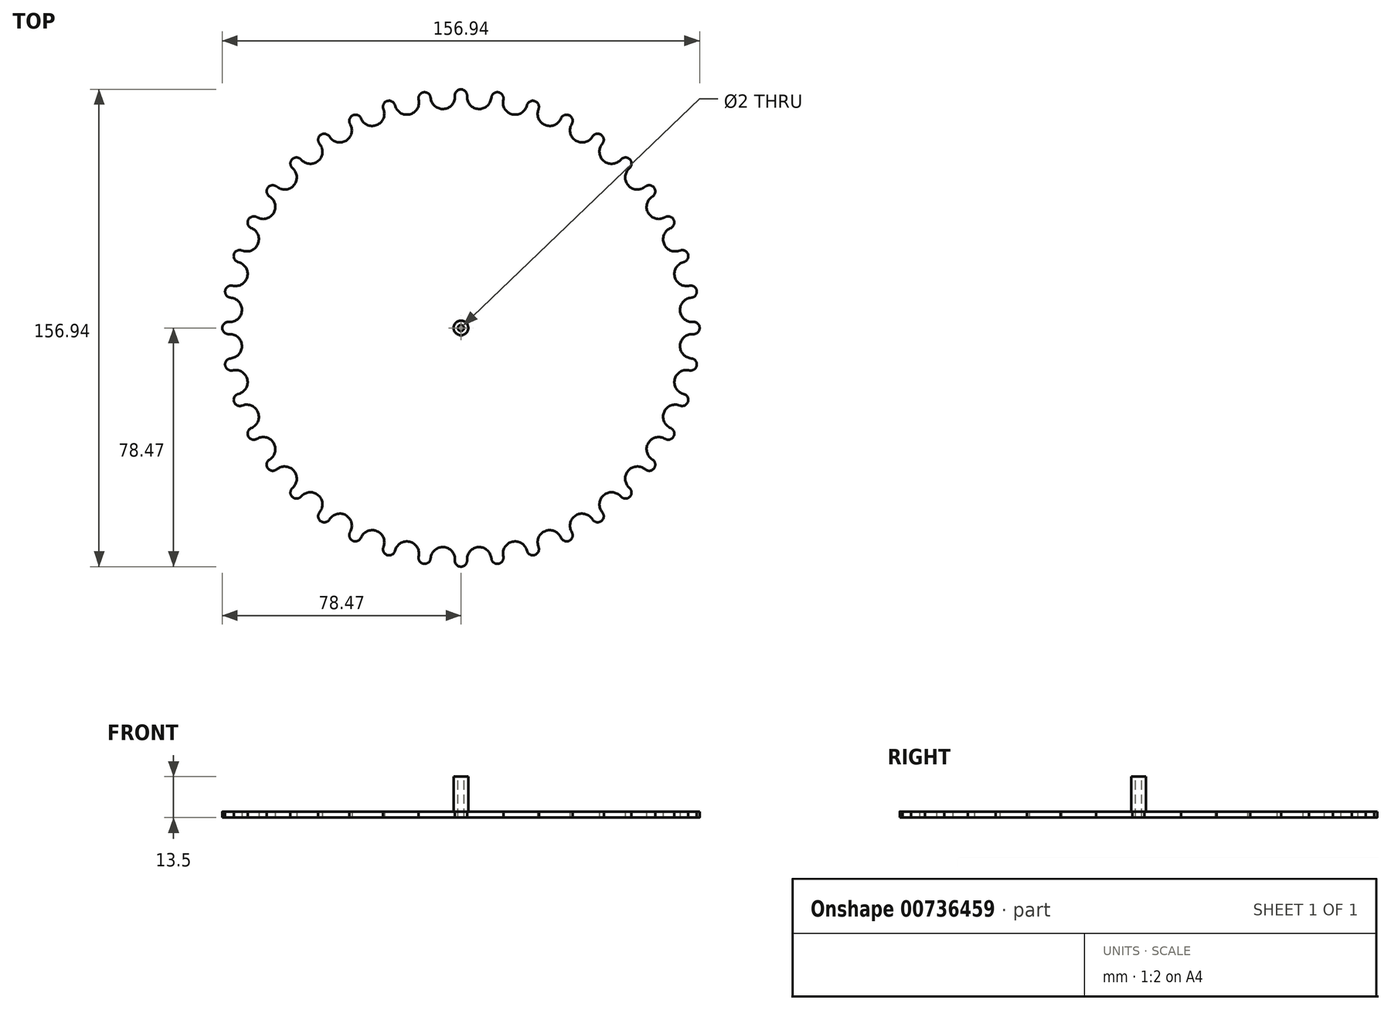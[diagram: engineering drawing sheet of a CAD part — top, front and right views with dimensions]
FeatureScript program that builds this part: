
annotation { "Feature Type Name" : "Feature", "Feature Type Description" : "" }
export const myFeature = defineFeature(function(context is Context, id is Id, definition is map)
    precondition{}
    {
        {
            var Q0;
            Q0=qCreatedBy(makeId("Top.planeOp"),FACE);
            var sketch = newSketch(context, id + "F0", { "sketchPlane" : qUnion([Q0])});
            skArc(sketch, "E0", {"start": v(2, 76.47) * mm, "mid": v(0, 78.47) * mm, "end": v(-2, 76.47) * mm});
            skLineSegment(sketch, "E1", {"start": v(2, 76.47) * mm, "end": v(2, 76) * mm});
            skLineSegment(sketch, "E2", {"start": v(-2, 76.47) * mm, "end": v(-2, 76) * mm});
            skLineSegment(sketch, "E3", {"start": v(-5.98, 76) * mm, "end": v(-5.67, 72.03) * mm, "construction": true});
            skArc(sketch, "E4", {"start": v(-5.67, 72.03) * mm, "mid": v(-3.06, 73.3) * mm, "end": v(-2, 76) * mm});
            skLineSegment(sketch, "E5", {"start": v(-5.67, 72.03) * mm, "end": v(-4.67, 72.11) * mm, "construction": true});
            skLineSegment(sketch, "E6", {"start": v(0, 0) * mm, "end": v(-5.67, 72.03) * mm});
            skCircle(sketch, "E7.cCircle", {"center": v(0, 0) * mm, "radius": 76.47 * mm, "construction": true});
            skLineSegment(sketch, "E7.0", {"start": v(0, 76.47) * mm, "end": v(11.96, 75.53) * mm, "construction": true});
            skLineSegment(sketch, "E7.1", {"start": v(11.96, 75.53) * mm, "end": v(23.63, 72.73) * mm, "construction": true});
            skLineSegment(sketch, "E7.2", {"start": v(23.63, 72.73) * mm, "end": v(34.72, 68.14) * mm, "construction": true});
            skLineSegment(sketch, "E7.3", {"start": v(34.72, 68.14) * mm, "end": v(44.95, 61.87) * mm, "construction": true});
            skLineSegment(sketch, "E7.4", {"start": v(44.95, 61.87) * mm, "end": v(54.07, 54.07) * mm, "construction": true});
            skLineSegment(sketch, "E7.5", {"start": v(54.07, 54.07) * mm, "end": v(61.87, 44.95) * mm, "construction": true});
            skLineSegment(sketch, "E7.6", {"start": v(61.87, 44.95) * mm, "end": v(68.14, 34.72) * mm, "construction": true});
            skLineSegment(sketch, "E7.7", {"start": v(68.14, 34.72) * mm, "end": v(72.73, 23.63) * mm, "construction": true});
            skLineSegment(sketch, "E7.8", {"start": v(72.73, 23.63) * mm, "end": v(75.53, 11.96) * mm, "construction": true});
            skLineSegment(sketch, "E7.9", {"start": v(75.53, 11.96) * mm, "end": v(76.47, 0) * mm, "construction": true});
            skLineSegment(sketch, "E7.10", {"start": v(76.47, 0) * mm, "end": v(75.53, -11.96) * mm, "construction": true});
            skLineSegment(sketch, "E7.11", {"start": v(75.53, -11.96) * mm, "end": v(72.73, -23.63) * mm, "construction": true});
            skLineSegment(sketch, "E7.12", {"start": v(72.73, -23.63) * mm, "end": v(68.14, -34.72) * mm, "construction": true});
            skLineSegment(sketch, "E7.13", {"start": v(68.14, -34.72) * mm, "end": v(61.87, -44.95) * mm, "construction": true});
            skLineSegment(sketch, "E7.14", {"start": v(61.87, -44.95) * mm, "end": v(54.07, -54.07) * mm, "construction": true});
            skLineSegment(sketch, "E7.15", {"start": v(54.07, -54.07) * mm, "end": v(44.95, -61.87) * mm, "construction": true});
            skLineSegment(sketch, "E7.16", {"start": v(44.95, -61.87) * mm, "end": v(34.72, -68.14) * mm, "construction": true});
            skLineSegment(sketch, "E7.17", {"start": v(34.72, -68.14) * mm, "end": v(23.63, -72.73) * mm, "construction": true});
            skLineSegment(sketch, "E7.18", {"start": v(23.63, -72.73) * mm, "end": v(11.96, -75.53) * mm, "construction": true});
            skLineSegment(sketch, "E7.19", {"start": v(11.96, -75.53) * mm, "end": v(0, -76.47) * mm, "construction": true});
            skLineSegment(sketch, "E7.20", {"start": v(0, -76.47) * mm, "end": v(-11.96, -75.53) * mm, "construction": true});
            skLineSegment(sketch, "E7.21", {"start": v(-11.96, -75.53) * mm, "end": v(-23.63, -72.73) * mm, "construction": true});
            skLineSegment(sketch, "E7.22", {"start": v(-23.63, -72.73) * mm, "end": v(-34.72, -68.14) * mm, "construction": true});
            skLineSegment(sketch, "E7.23", {"start": v(-34.72, -68.14) * mm, "end": v(-44.95, -61.87) * mm, "construction": true});
            skLineSegment(sketch, "E7.24", {"start": v(-44.95, -61.87) * mm, "end": v(-54.07, -54.07) * mm, "construction": true});
            skLineSegment(sketch, "E7.25", {"start": v(-54.07, -54.07) * mm, "end": v(-61.87, -44.95) * mm, "construction": true});
            skLineSegment(sketch, "E7.26", {"start": v(-61.87, -44.95) * mm, "end": v(-68.14, -34.72) * mm, "construction": true});
            skLineSegment(sketch, "E7.27", {"start": v(-68.14, -34.72) * mm, "end": v(-72.73, -23.63) * mm, "construction": true});
            skLineSegment(sketch, "E7.28", {"start": v(-72.73, -23.63) * mm, "end": v(-75.53, -11.96) * mm, "construction": true});
            skLineSegment(sketch, "E7.29", {"start": v(-75.53, -11.96) * mm, "end": v(-76.47, 0) * mm, "construction": true});
            skLineSegment(sketch, "E7.30", {"start": v(-76.47, 0) * mm, "end": v(-75.53, 11.96) * mm, "construction": true});
            skLineSegment(sketch, "E7.31", {"start": v(-75.53, 11.96) * mm, "end": v(-72.73, 23.63) * mm, "construction": true});
            skLineSegment(sketch, "E7.32", {"start": v(-72.73, 23.63) * mm, "end": v(-68.14, 34.72) * mm, "construction": true});
            skLineSegment(sketch, "E7.33", {"start": v(-68.14, 34.72) * mm, "end": v(-61.87, 44.95) * mm, "construction": true});
            skLineSegment(sketch, "E7.34", {"start": v(-61.87, 44.95) * mm, "end": v(-54.07, 54.07) * mm, "construction": true});
            skLineSegment(sketch, "E7.35", {"start": v(-54.07, 54.07) * mm, "end": v(-44.95, 61.87) * mm, "construction": true});
            skLineSegment(sketch, "E7.36", {"start": v(-44.95, 61.87) * mm, "end": v(-34.72, 68.14) * mm, "construction": true});
            skLineSegment(sketch, "E7.37", {"start": v(-34.72, 68.14) * mm, "end": v(-23.63, 72.73) * mm, "construction": true});
            skLineSegment(sketch, "E7.38", {"start": v(-23.63, 72.73) * mm, "end": v(-11.96, 75.53) * mm, "construction": true});
            skLineSegment(sketch, "E7.39", {"start": v(-11.96, 75.53) * mm, "end": v(0, 76.47) * mm, "construction": true});
            skArc(sketch, "E8", {"start": v(2, 76) * mm, "mid": v(3.06, 73.3) * mm, "end": v(5.67, 72.03) * mm});
            skLineSegment(sketch, "E9", {"start": v(5.98, 76) * mm, "end": v(5.67, 72.03) * mm, "construction": true});
            skLineSegment(sketch, "E10", {"start": v(5.67, 72.03) * mm, "end": v(4.67, 72.11) * mm, "construction": true});
            skLineSegment(sketch, "E11", {"start": v(0, 0) * mm, "end": v(5.67, 72.03) * mm});
            skSolve(sketch);
        }
        {
            var Q0;
            Q0=qSketchRegion(id+"F0",true);
            extrude(context, id + "F1", {"entities" : qUnion([Q0]), "endBound" : BoundingType.SYMMETRIC, "depth" : 2 * mm, "offsetDistance" : 25 * mm});
        }
        {
            var Q0;
            Q0=makeQuery(id+"F1.opExtrude","SWEPT_BODY",BODY,{"disambiguationData":[OSD([sQuery(id+"F0.wireOp",EDGE,"E0"),sQuery(id+"F0.wireOp",EDGE,"E1"),sQuery(id+"F0.wireOp",EDGE,"E2"),sQuery(id+"F0.wireOp",EDGE,"E4"),sQuery(id+"F0.wireOp",EDGE,"W5vAHDtY-rvEH-ViCa-0FPo-8mxshjeyYw7U"),sQuery(id+"F0.wireOp",EDGE,"J2sdAHte-avJF-ZFeu-cnuh-1Djj5LRI9oCG"),sQuery(id+"F0.wireOp",EDGE,"E6")])]});
            var Q1;
            Q1=makeQuery(id+"F1.opExtrude","SWEPT_EDGE",EDGE,{"disambiguationData":[OSD([sQuery(id+"F0.wireOp",EDGE,"E6"),sQuery(id+"F0.wireOp",EDGE,"E11")])]});
            circularPattern(context, id + "F2", {"operationType" : NewBodyOperationType.ADD, "entities" : qUnion([Q0]), "axis" : qUnion([Q1]), "angle" : 360 * degree, "instanceCount" : 40, "equalSpace" : true});
        }
        {
            var Q0;
            Q0=qCreatedBy(makeId("Top.planeOp"),FACE);
            var sketch = newSketch(context, id + "F3", { "sketchPlane" : qUnion([Q0])});
            skCircle(sketch, "E12", {"center": v(0, 0) * mm, "radius": 2.4 * mm});
            skSolve(sketch);
        }
        {
            var Q0;
            Q0=qSketchRegion(id+"F3",true);
            extrude(context, id + "F4", {"entities" : qUnion([Q0]), "operationType" : NewBodyOperationType.ADD, "depth" : 12.5 * mm, "offsetDistance" : 25 * mm});
        }
        {
            var Q0;
            Q0=makeQuery(id+"F4.opExtrude","CAP_FACE",FACE,{"disambiguationData":[OSD([sQuery(id+"F3.wireOp",EDGE,"E12")])],"isStart":false});
            var sketch = newSketch(context, id + "F5", { "sketchPlane" : qUnion([Q0])});
            skCircle(sketch, "E13", {"center": v(0, 0) * mm, "radius": 1 * mm});
            skSolve(sketch);
        }
        {
            var Q0;
            Q0=qSketchRegion(id+"F5",true);
            extrude(context, id + "F6", {"entities" : qUnion([Q0]), "operationType" : NewBodyOperationType.REMOVE, "endBound" : BoundingType.THROUGH_ALL, "oppositeDirection" : true, "depth" : 25 * mm, "offsetDistance" : 25 * mm});
        }
    });
